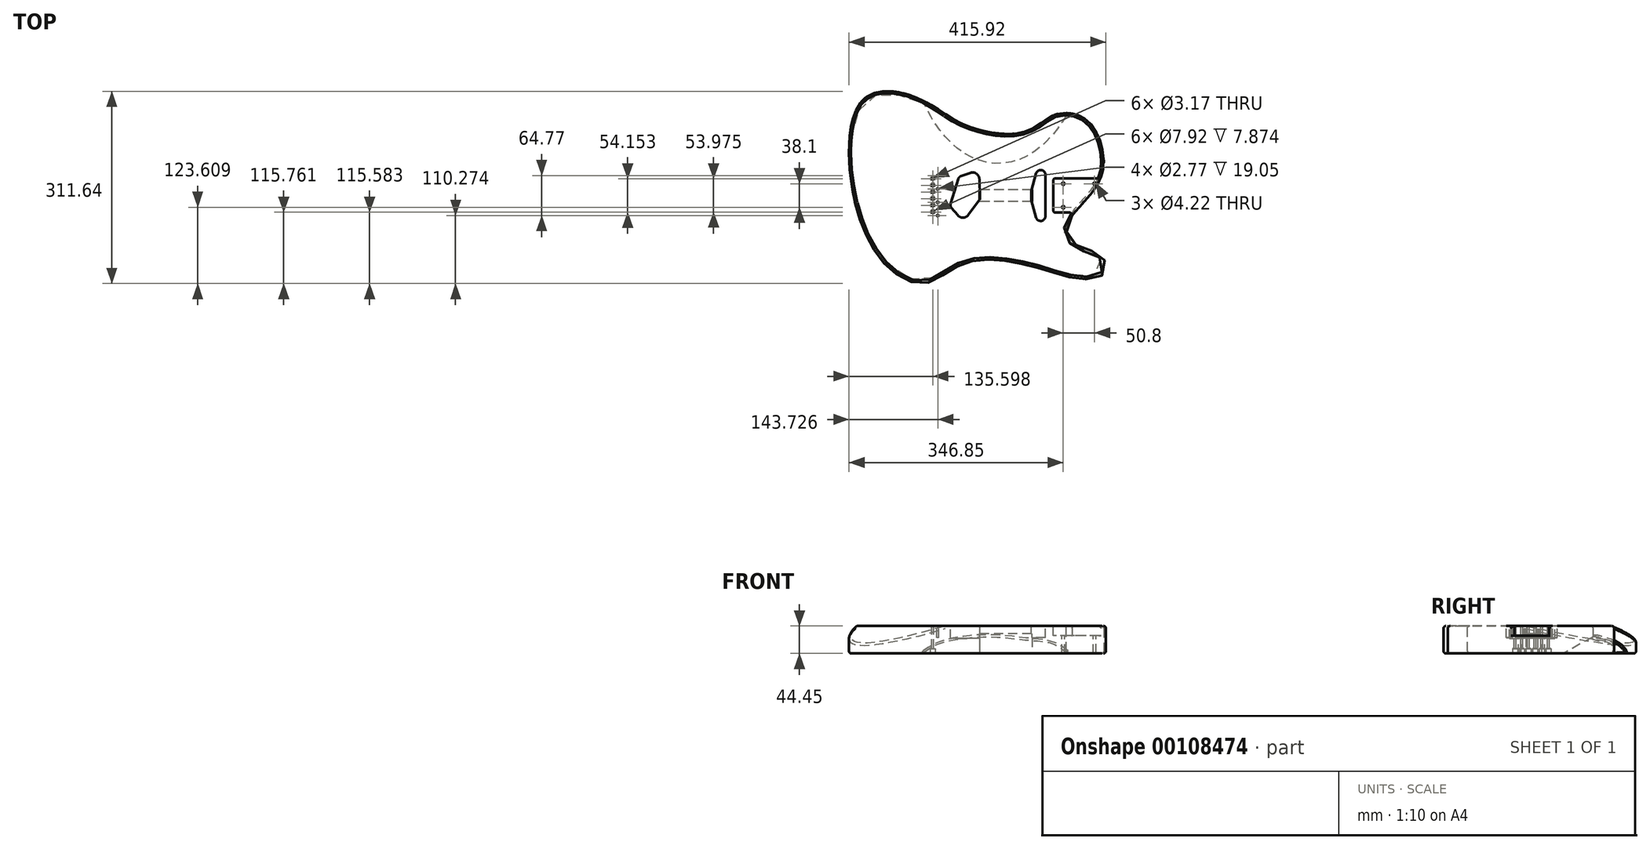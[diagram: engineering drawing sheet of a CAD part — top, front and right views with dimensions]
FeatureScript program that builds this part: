
annotation { "Feature Type Name" : "Feature", "Feature Type Description" : "" }
export const myFeature = defineFeature(function(context is Context, id is Id, definition is map)
    precondition{}
    {
        {
            var Q0;
            Q0=qCreatedBy(makeId("Top.planeOp"),FACE);
            var sketch = newSketch(context, id + "F0", { "sketchPlane" : qUnion([Q0])});
            skFitSpline(sketch, "E0", {"points": [v(437.8, 38.75) * mm, v(393.42, 31.36) * mm, v(332.63, 48.34) * mm, v(216.68, 57.77) * mm, v(157.53, 25.75) * mm, v(111.17, 32.37) * mm, v(43.17, 126.41) * mm, v(48.1, 320.57) * mm, v(140.27, 321.8) * mm, v(210.75, 280.95) * mm, v(303.47, 267.33) * mm, v(344.28, 288.4) * mm, v(367.26, 298.72) * mm, v(405.94, 290.75) * mm, v(432.67, 250.93) * mm, v(432.44, 193.48) * mm, v(390.48, 137.92) * mm, v(377.35, 108.2) * mm, v(396.27, 83.12) * mm, v(433.81, 68.33) * mm, v(437.8, 38.75) * mm]});
            skLineSegment(sketch, "E1", {"start": v(432.44, 193.48) * mm, "end": v(432.44, 137.92) * mm});
            skLineSegment(sketch, "E2", {"start": v(390.48, 137.92) * mm, "end": v(432.44, 137.92) * mm});
            skSolve(sketch);
        }
        {
            var Q0;
            Q0=makeQuery(id+"F0.imprint","IMPRINT",FACE,{"disambiguationData":[TD([[makeQuery(id+"F0.imprint","IMPRINT",EDGE,{"derivedFrom":sQuery(id+"F0.wireOp",EDGE,"E0")}),-1.0]])]});
            extrude(context, id + "F1", {"entities" : qUnion([Q0]), "depth" : 44.45 * mm});
        }
        {
            var Q0;
            Q0=qCreatedBy(makeId("Front.planeOp"),FACE);
            cPlane(context, id + "F2", {"entities" : qUnion([Q0]), "cplaneType" : CPlaneType.OFFSET, "offset" : 228.6 * mm, "oppositeDirection" : true, "width" : 152.4 * mm, "height" : 152.4 * mm});
        }
        {
            var Q0;
            Q0=qCreatedBy(id+"F2.planeOp",FACE);
            var sketch = newSketch(context, id + "F3", { "sketchPlane" : qUnion([Q0])});
            skLineSegment(sketch, "E3", {"start": v(7.53, 44.67) * mm, "end": v(7.53, 0) * mm});
            skSolve(sketch);
        }
        {
            var Q0;
            Q0=sQuery(id+"F3.wireOp",EDGE,"E3");
            var Q1;
            Q1=qCreatedBy(id+"F2.planeOp",FACE);
            cPlane(context, id + "F4", {"entities" : qUnion([Q0, Q1]), "cplaneType" : CPlaneType.LINE_ANGLE, "offset" : 25.4 * mm, "angle" : 45 * degree, "width" : 152.4 * mm, "height" : 152.4 * mm});
        }
        {
            var Q0;
            Q0=qCreatedBy(id+"F4.planeOp",FACE);
            var sketch = newSketch(context, id + "F5", { "sketchPlane" : qUnion([Q0])});
            skLineSegment(sketch, "E4", {"start": v(72.23, 46.82) * mm, "end": v(212.01, 11.13) * mm});
            skLineSegment(sketch, "E5.bottom", {"start": v(72.23, 46.82) * mm, "end": v(214.33, 45.27) * mm});
            skLineSegment(sketch, "E5.right", {"start": v(214.33, 45.27) * mm, "end": v(212.01, 11.13) * mm});
            skSolve(sketch);
        }
        {
            var Q0;
            Q0 = qSketchRegion(id + "F5", true);
            extrude(context, id + "F6", {"entities" : qUnion([Q0]), "operationType" : NewBodyOperationType.REMOVE, "endBound" : BoundingType.SYMMETRIC, "oppositeDirection" : true, "depth" : 508 * mm});
        }
        {
            var Q0;
            Q0=qCreatedBy(makeId("Right.planeOp"),FACE);
            cPlane(context, id + "F7", {"entities" : qUnion([Q0]), "cplaneType" : CPlaneType.OFFSET, "offset" : 266.7 * mm, "width" : 152.4 * mm, "height" : 152.4 * mm});
        }
        {
            var Q0;
            Q0=qCreatedBy(id+"F7.planeOp",FACE);
            var sketch = newSketch(context, id + "F8", { "sketchPlane" : qUnion([Q0])});
            skLineSegment(sketch, "E6", {"start": v(319.77, 57.36) * mm, "end": v(216.72, 0) * mm});
            skLineSegment(sketch, "E7", {"start": v(319.77, 57.36) * mm, "end": v(326.36, -7.5) * mm});
            skLineSegment(sketch, "E8", {"start": v(326.36, -7.5) * mm, "end": v(216.72, 0) * mm});
            skSolve(sketch);
        }
        {
            var Q0;
            Q0=qCreatedBy(id+"F7.planeOp",FACE);
            var sketch = newSketch(context, id + "F9", { "sketchPlane" : qUnion([Q0])});
            skLineSegment(sketch, "E9", {"start": v(470.03, -32.93) * mm, "end": v(353.93, -132.78) * mm});
            skSolve(sketch);
        }
        {
            var Q0;
            Q0=makeQuery(id+"F8.imprint","IMPRINT",FACE,{"disambiguationData":[TD([[makeQuery(id+"F8.imprint","IMPRINT",EDGE,{"derivedFrom":sQuery(id+"F8.wireOp",EDGE,"E6")}),1.0]])]});
            var Q1;
            Q1=sQuery(id+"F9.wireOp",EDGE,"E9");
            revolve(context, id + "F10", {"operationType" : NewBodyOperationType.REMOVE, "entities" : qUnion([Q0]), "axis" : qUnion([Q1]), "revolveType" : RevolveType.FULL, "oppositeDirection" : true});
        }
        {
            var Q0;
            Q0=makeQuery(id+"F1.opExtrude","CAP_FACE",FACE,{"disambiguationData":[OSD([sQuery(id+"F0.wireOp",EDGE,"E0"),sQuery(id+"F0.wireOp",EDGE,"E1"),sQuery(id+"F0.wireOp",EDGE,"E2")])],"isStart":false});
            var sketch = newSketch(context, id + "F11", { "sketchPlane" : qUnion([Q0])});
            skLineSegment(sketch, "E10.bottom", {"start": v(432.44, 137.92) * mm, "end": v(359.42, 137.92) * mm});
            skLineSegment(sketch, "E10.top", {"start": v(432.44, 193.48) * mm, "end": v(359.42, 193.48) * mm});
            skLineSegment(sketch, "E10.left", {"start": v(432.44, 137.92) * mm, "end": v(432.44, 193.48) * mm});
            skLineSegment(sketch, "E10.right", {"start": v(356.24, 141.1) * mm, "end": v(356.24, 190.3) * mm});
            skPoint(sketch, "E11.visualSharp", {"position": v(356.24, 193.48) * mm});
            skArc(sketch, "E11.filletArc", {"start": v(359.42, 193.48) * mm, "mid": v(357.17, 192.55) * mm, "end": v(356.24, 190.3) * mm});
            skPoint(sketch, "E12.visualSharp", {"position": v(356.24, 137.92) * mm});
            skArc(sketch, "E12.filletArc", {"start": v(356.24, 141.1) * mm, "mid": v(357.17, 138.85) * mm, "end": v(359.42, 137.92) * mm});
            skSolve(sketch);
        }
        {
            var Q0;
            Q0=makeQuery(id+"F11.imprint","IMPRINT",FACE,{"disambiguationData":[TD([[makeQuery(id+"F11.imprint","IMPRINT",EDGE,{"derivedFrom":sQuery(id+"F11.wireOp",EDGE,"E10.right")}),-1.0]])]});
            extrude(context, id + "F12", {"entities" : qUnion([Q0]), "operationType" : NewBodyOperationType.REMOVE, "oppositeDirection" : true, "depth" : 15.88 * mm});
        }
        {
            var Q0;
            Q0=makeQuery(id+"F1.opExtrude","CAP_FACE",FACE,{"disambiguationData":[OSD([sQuery(id+"F0.wireOp",EDGE,"E0"),sQuery(id+"F0.wireOp",EDGE,"E1"),sQuery(id+"F0.wireOp",EDGE,"E2")])],"isStart":false});
            var sketch = newSketch(context, id + "F13", { "sketchPlane" : qUnion([Q0])});
            skCircle(sketch, "E13", {"center": v(169.05, 198.08) * mm, "radius": 1.38 * mm});
            skCircle(sketch, "E14", {"center": v(169.05, 176.5) * mm, "radius": 1.38 * mm});
            skCircle(sketch, "E15", {"center": v(169.05, 154.9) * mm, "radius": 1.38 * mm});
            skCircle(sketch, "E16", {"center": v(169.05, 133.31) * mm, "radius": 1.38 * mm});
            skLineSegment(sketch, "E17", {"start": v(356.24, 165.7) * mm, "end": v(160.53, 165.7) * mm, "construction": true});
            skPoint(sketch, "E17.endSnap0", {"position": v(356.24, 165.7) * mm});
            skSolve(sketch);
        }
        {
            var Q0;
            Q0 = qSketchRegion(id + "F13", true);
            extrude(context, id + "F14", {"entities" : qUnion([Q0]), "operationType" : NewBodyOperationType.REMOVE, "oppositeDirection" : true, "depth" : 19.05 * mm});
        }
        {
            var Q0;
            Q0=makeQuery(id+"F1.opExtrude","CAP_FACE",FACE,{"disambiguationData":[OSD([sQuery(id+"F0.wireOp",EDGE,"E0"),sQuery(id+"F0.wireOp",EDGE,"E1"),sQuery(id+"F0.wireOp",EDGE,"E2")])],"isStart":false});
            var sketch = newSketch(context, id + "F15", { "sketchPlane" : qUnion([Q0])});
            skCircle(sketch, "E18", {"center": v(160.92, 192.78) * mm, "radius": 1.59 * mm});
            skLineSegment(sketch, "E19.direction1", {"start": v(160.92, 192.78) * mm, "end": v(162.5, 192.78) * mm, "construction": true});
            skLineSegment(sketch, "E20", {"start": v(356.24, 165.7) * mm, "end": v(102.22, 165.7) * mm, "construction": true});
            skLineSegment(sketch, "E21", {"start": v(169.05, 198.08) * mm, "end": v(169.05, 133.31) * mm, "construction": true});
            skCircle(sketch, "E22.0.1.0", {"center": v(160.92, 181.95) * mm, "radius": 1.59 * mm});
            skCircle(sketch, "E22.0.2.0", {"center": v(160.92, 171.11) * mm, "radius": 1.59 * mm});
            skCircle(sketch, "E22.0.3.0", {"center": v(160.92, 160.28) * mm, "radius": 1.59 * mm});
            skCircle(sketch, "E22.0.4.0", {"center": v(160.92, 149.45) * mm, "radius": 1.59 * mm});
            skCircle(sketch, "E22.0.5.0", {"center": v(160.92, 138.62) * mm, "radius": 1.59 * mm});
            skLineSegment(sketch, "E22.direction1", {"start": v(160.92, 192.78) * mm, "end": v(186.32, 192.78) * mm, "construction": true});
            skLineSegment(sketch, "E22.direction2", {"start": v(160.92, 192.78) * mm, "end": v(160.92, 181.95) * mm, "construction": true});
            skSolve(sketch);
        }
        {
            var Q0;
            Q0 = qSketchRegion(id + "F15", true);
            extrude(context, id + "F16", {"entities" : qUnion([Q0]), "operationType" : NewBodyOperationType.REMOVE, "endBound" : BoundingType.THROUGH_ALL, "oppositeDirection" : true, "depth" : 25.4 * mm});
        }
        {
            var Q0;
            Q0=makeQuery(id+"F1.opExtrude","CAP_FACE",FACE,{"disambiguationData":[OSD([sQuery(id+"F0.wireOp",EDGE,"E0"),sQuery(id+"F0.wireOp",EDGE,"E1"),sQuery(id+"F0.wireOp",EDGE,"E2")])],"isStart":true});
            var sketch = newSketch(context, id + "F17", { "sketchPlane" : qUnion([Q0])});
            skCircle(sketch, "E23", {"center": v(160.92, -192.78) * mm, "radius": 3.96 * mm});
            skCircle(sketch, "E24.0.1.0", {"center": v(160.92, -181.98) * mm, "radius": 3.96 * mm});
            skCircle(sketch, "E24.0.2.0", {"center": v(160.92, -171.19) * mm, "radius": 3.96 * mm});
            skCircle(sketch, "E24.0.3.0", {"center": v(160.92, -160.4) * mm, "radius": 3.96 * mm});
            skCircle(sketch, "E24.0.4.0", {"center": v(160.92, -149.6) * mm, "radius": 3.96 * mm});
            skCircle(sketch, "E24.0.5.0", {"center": v(160.92, -138.8) * mm, "radius": 3.96 * mm});
            skLineSegment(sketch, "E24.direction1", {"start": v(160.92, -192.78) * mm, "end": v(181.38, -192.78) * mm, "construction": true});
            skLineSegment(sketch, "E24.direction2", {"start": v(160.92, -181.98) * mm, "end": v(160.92, -192.78) * mm, "construction": true});
            skSolve(sketch);
        }
        {
            var Q0;
            Q0 = qSketchRegion(id + "F17", true);
            extrude(context, id + "F18", {"entities" : qUnion([Q0]), "operationType" : NewBodyOperationType.REMOVE, "oppositeDirection" : true, "depth" : 7.87 * mm});
        }
        {
            var Q0;
            Q0=makeQuery(id+"F1.opExtrude","CAP_FACE",FACE,{"disambiguationData":[OSD([sQuery(id+"F0.wireOp",EDGE,"E0"),sQuery(id+"F0.wireOp",EDGE,"E1"),sQuery(id+"F0.wireOp",EDGE,"E2")])],"isStart":false});
            var sketch = newSketch(context, id + "F19", { "sketchPlane" : qUnion([Q0])});
            skArc(sketch, "E25", {"start": v(236.4, 192.48) * mm, "mid": v(231.68, 201.04) * mm, "end": v(222, 202.4) * mm});
            skArc(sketch, "E26", {"start": v(201.44, 133.57) * mm, "mid": v(210.11, 129.73) * mm, "end": v(218.52, 134.12) * mm});
            skArc(sketch, "E27", {"start": v(206.93, 197.34) * mm, "mid": v(204.27, 195.67) * mm, "end": v(202.65, 192.96) * mm});
            skArc(sketch, "E28", {"start": v(189.87, 152.02) * mm, "mid": v(189.7, 148.67) * mm, "end": v(191.17, 145.66) * mm});
            skLineSegment(sketch, "E29", {"start": v(222, 202.4) * mm, "end": v(206.93, 197.34) * mm});
            skLineSegment(sketch, "E30", {"start": v(201.44, 133.57) * mm, "end": v(191.17, 145.66) * mm});
            skPoint(sketch, "E31.center.orphan", {"position": v(230.87, 162) * mm});
            skArc(sketch, "E32", {"start": v(236.27, 157.97) * mm, "mid": v(237.3, 160) * mm, "end": v(237.6, 162.26) * mm});
            skLineSegment(sketch, "E33", {"start": v(236.4, 192.48) * mm, "end": v(237.6, 162.26) * mm});
            skLineSegment(sketch, "E34", {"start": v(236.27, 157.97) * mm, "end": v(218.52, 134.12) * mm});
            skLineSegment(sketch, "E35", {"start": v(202.65, 192.96) * mm, "end": v(189.87, 152.02) * mm});
            skLineSegment(sketch, "E36", {"start": v(169.05, 133.31) * mm, "end": v(169.05, 198.08) * mm, "construction": true});
            skLineSegment(sketch, "E37", {"start": v(169.05, 165.7) * mm, "end": v(249.84, 165.7) * mm, "construction": true});
            skLineSegment(sketch, "E38", {"start": v(160.92, 138.62) * mm, "end": v(160.92, 192.78) * mm, "construction": true});
            skSolve(sketch);
        }
        {
            var Q0;
            Q0=makeQuery(id+"F19.imprint","IMPRINT",FACE,{"disambiguationData":[TD([[makeQuery(id+"F19.imprint","IMPRINT",EDGE,{"derivedFrom":sQuery(id+"F19.wireOp",EDGE,"E25")}),1.0]])]});
            extrude(context, id + "F20", {"entities" : qUnion([Q0]), "operationType" : NewBodyOperationType.REMOVE, "oppositeDirection" : true, "depth" : 20.32 * mm});
        }
        {
            var Q0;
            Q0=makeQuery(id+"F12.boolean.opBoolean","COPY",FACE,{"derivedFrom":makeQuery(id+"F12.opExtrude","CAP_FACE",FACE,{"disambiguationData":[OSD([sQuery(id+"F11.wireOp",EDGE,"E10.bottom"),sQuery(id+"F11.wireOp",EDGE,"E10.top"),sQuery(id+"F11.wireOp",EDGE,"E10.left"),sQuery(id+"F11.wireOp",EDGE,"E10.right"),sQuery(id+"F11.wireOp",EDGE,"E11.filletArc"),sQuery(id+"F11.wireOp",EDGE,"E12.filletArc")])],"isStart":false})});
            var sketch = newSketch(context, id + "F21", { "sketchPlane" : qUnion([Q0])});
            skCircle(sketch, "E39", {"center": v(372.17, 184.75) * mm, "radius": 2.1 * mm});
            skLineSegment(sketch, "E40", {"start": v(432.44, 165.7) * mm, "end": v(356.24, 165.7) * mm, "construction": true});
            skCircle(sketch, "E41.0.1.0", {"center": v(372.17, 146.65) * mm, "radius": 2.1 * mm});
            skCircle(sketch, "E41.1.0.0", {"center": v(422.97, 184.75) * mm, "radius": 2.1 * mm});
            skCircle(sketch, "E41.1.1.0", {"center": v(422.97, 146.65) * mm, "radius": 2.1 * mm});
            skLineSegment(sketch, "E41.direction1", {"start": v(372.17, 184.75) * mm, "end": v(422.97, 184.75) * mm, "construction": true});
            skLineSegment(sketch, "E41.direction2", {"start": v(372.17, 184.75) * mm, "end": v(372.17, 146.65) * mm, "construction": true});
            skSolve(sketch);
        }
        {
            var Q0;
            Q0 = qSketchRegion(id + "F21", true);
            extrude(context, id + "F22", {"entities" : qUnion([Q0]), "operationType" : NewBodyOperationType.REMOVE, "endBound" : BoundingType.THROUGH_ALL, "oppositeDirection" : true, "depth" : 25.4 * mm});
        }
        {
            var Q0;
            {var subQ0=sQuery(id+"F0.wireOp",EDGE,"E0");var subQ1=sQuery(id+"F0.wireOp",EDGE,"E1");Q0=makeQuery(id+"F6.boolean.opBoolean","SPLIT",EDGE,{"disambiguationData":[TD([makeQuery(id+"F1.opExtrude","SWEPT_FACE",FACE,{"disambiguationData":[OSD([subQ1])]})])],"derivedFrom":makeQuery(id+"F1.opExtrude","CAP_EDGE",EDGE,{"disambiguationData":[OSD([subQ0])],"isStart":false})});}
            var Q1;
            Q1=makeQuery(id+"F10.boolean.opBoolean","INTERSECT",EDGE,{"derivedFrom":[makeQuery(id+"F1.opExtrude","SWEPT_FACE",FACE,{"disambiguationData":[OSD([sQuery(id+"F0.wireOp",EDGE,"E0")])]}),makeQuery(id+"F10.opRevolve","SWEPT_FACE",FACE,{"disambiguationData":[OSD([sQuery(id+"F8.wireOp",EDGE,"E6")])]})]});
            var Q2;
            Q2=makeQuery(id+"F12.boolean.opBoolean","SPLIT",EDGE,{"derivedFrom":makeQuery(id+"F1.opExtrude","SWEPT_EDGE",EDGE,{"disambiguationData":[OSD([sQuery(id+"F0.wireOp",EDGE,"E0"),sQuery(id+"F0.wireOp",EDGE,"E1")])]})});
            var Q3;
            {var subQ0=sQuery(id+"F0.wireOp",EDGE,"E0");var subQ1=sQuery(id+"F0.wireOp",EDGE,"E2");Q3=makeQuery(id+"F10.boolean.opBoolean","SPLIT",EDGE,{"disambiguationData":[TD([makeQuery(id+"F1.opExtrude","SWEPT_FACE",FACE,{"disambiguationData":[OSD([subQ1])]})])],"derivedFrom":makeQuery(id+"F1.opExtrude","CAP_EDGE",EDGE,{"disambiguationData":[OSD([subQ0])],"isStart":true})});}
            var Q4;
            Q4=makeQuery(id+"F1.opExtrude","CAP_EDGE",EDGE,{"disambiguationData":[OSD([sQuery(id+"F0.wireOp",EDGE,"E1")])],"isStart":true});
            var Q5;
            Q5=makeQuery(id+"F1.opExtrude","SWEPT_EDGE",EDGE,{"disambiguationData":[OSD([sQuery(id+"F0.wireOp",EDGE,"E1"),sQuery(id+"F0.wireOp",EDGE,"E2")])]});
            var Q6;
            Q6=makeQuery(id+"F6.boolean.opBoolean","INTERSECT",EDGE,{"derivedFrom":[makeQuery(id+"F1.opExtrude","CAP_FACE",FACE,{"disambiguationData":[OSD([sQuery(id+"F0.wireOp",EDGE,"E0"),sQuery(id+"F0.wireOp",EDGE,"E1"),sQuery(id+"F0.wireOp",EDGE,"E2")])],"isStart":false}),makeQuery(id+"F6.opExtrude","SWEPT_FACE",FACE,{"disambiguationData":[OSD([sQuery(id+"F5.wireOp",EDGE,"E4")])]})]});
            var Q7;
            Q7=makeQuery(id+"F6.boolean.opBoolean","INTERSECT",EDGE,{"derivedFrom":[makeQuery(id+"F1.opExtrude","SWEPT_FACE",FACE,{"disambiguationData":[OSD([sQuery(id+"F0.wireOp",EDGE,"E0")])]}),makeQuery(id+"F6.opExtrude","SWEPT_FACE",FACE,{"disambiguationData":[OSD([sQuery(id+"F5.wireOp",EDGE,"E4")])]})]});
            var Q8;
            {var subQ0=sQuery(id+"F0.wireOp",EDGE,"E0");var subQ1=sQuery(id+"F0.wireOp",EDGE,"E1");Q8=makeQuery(id+"F10.boolean.opBoolean","SPLIT",EDGE,{"disambiguationData":[TD([makeQuery(id+"F1.opExtrude","SWEPT_FACE",FACE,{"disambiguationData":[OSD([subQ1])]})])],"derivedFrom":makeQuery(id+"F1.opExtrude","CAP_EDGE",EDGE,{"disambiguationData":[OSD([subQ0])],"isStart":true})});}
            var Q9;
            {var subQ0=sQuery(id+"F0.wireOp",EDGE,"E0");var subQ1=sQuery(id+"F0.wireOp",EDGE,"E2");Q9=makeQuery(id+"F6.boolean.opBoolean","SPLIT",EDGE,{"disambiguationData":[TD([makeQuery(id+"F1.opExtrude","SWEPT_FACE",FACE,{"disambiguationData":[OSD([subQ1])]})])],"derivedFrom":makeQuery(id+"F1.opExtrude","CAP_EDGE",EDGE,{"disambiguationData":[OSD([subQ0])],"isStart":false})});}
            var Q10;
            Q10=makeQuery(id+"F10.boolean.opBoolean","INTERSECT",EDGE,{"derivedFrom":[makeQuery(id+"F1.opExtrude","CAP_FACE",FACE,{"disambiguationData":[OSD([sQuery(id+"F0.wireOp",EDGE,"E0"),sQuery(id+"F0.wireOp",EDGE,"E1"),sQuery(id+"F0.wireOp",EDGE,"E2")])],"isStart":true}),makeQuery(id+"F10.opRevolve","SWEPT_FACE",FACE,{"disambiguationData":[OSD([sQuery(id+"F8.wireOp",EDGE,"E6")])]})]});
            var Q11;
            Q11=makeQuery(id+"F1.opExtrude","CAP_EDGE",EDGE,{"disambiguationData":[OSD([sQuery(id+"F0.wireOp",EDGE,"E2")])],"isStart":true});
            fillet(context, id + "F23", {"entities" : qUnion([Q0, Q1, Q2, Q3, Q4, Q5, Q6, Q7, Q8, Q9, Q10, Q11]), "radius" : 3.8 * mm, "tangentPropagation" : true, "allowEdgeOverflow" : false});
        }
        {
            var Q0;
            Q0=makeQuery(id+"F1.opExtrude","CAP_FACE",FACE,{"disambiguationData":[OSD([sQuery(id+"F0.wireOp",EDGE,"E0"),sQuery(id+"F0.wireOp",EDGE,"E1"),sQuery(id+"F0.wireOp",EDGE,"E2")])],"isStart":false});
            var sketch = newSketch(context, id + "F24", { "sketchPlane" : qUnion([Q0])});
            skLineSegment(sketch, "E42.right", {"start": v(343.29, 199.35) * mm, "end": v(343.29, 132.04) * mm});
            skArc(sketch, "E43", {"start": v(343.29, 199.35) * mm, "mid": v(336.71, 206.9) * mm, "end": v(328.33, 201.42) * mm});
            skArc(sketch, "E44", {"start": v(328.33, 129.98) * mm, "mid": v(336.71, 124.5) * mm, "end": v(343.29, 132.04) * mm});
            skLineSegment(sketch, "E45", {"start": v(356.24, 165.7) * mm, "end": v(275.02, 165.7) * mm, "construction": true});
            skLineSegment(sketch, "E46", {"start": v(320.43, 158.08) * mm, "end": v(328.33, 129.98) * mm});
            skLineSegment(sketch, "E47", {"start": v(320.43, 173.32) * mm, "end": v(328.33, 201.42) * mm});
            skLineSegment(sketch, "E48", {"start": v(320.43, 173.32) * mm, "end": v(320.43, 158.08) * mm});
            skPoint(sketch, "E49.orphan", {"position": v(328.05, 199.35) * mm});
            skPoint(sketch, "E50.orphan", {"position": v(328.05, 132.04) * mm});
            skSolve(sketch);
        }
        {
            var Q0;
            Q0 = qSketchRegion(id + "F24", true);
            extrude(context, id + "F25", {"entities" : qUnion([Q0]), "operationType" : NewBodyOperationType.REMOVE, "oppositeDirection" : true, "depth" : 19.05 * mm});
        }
        {
            var Q0;
            Q0=makeQuery(id+"F1.opExtrude","CAP_FACE",FACE,{"disambiguationData":[OSD([sQuery(id+"F0.wireOp",EDGE,"E0"),sQuery(id+"F0.wireOp",EDGE,"E1"),sQuery(id+"F0.wireOp",EDGE,"E2")])],"isStart":true});
            var sketch = newSketch(context, id + "F26", { "sketchPlane" : qUnion([Q0])});
            skLineSegment(sketch, "E51.bottom", {"start": v(321.95, -156.17) * mm, "end": v(236.86, -156.17) * mm});
            skLineSegment(sketch, "E51.top", {"start": v(321.95, -175.22) * mm, "end": v(236.86, -175.22) * mm});
            skLineSegment(sketch, "E51.left", {"start": v(321.95, -156.17) * mm, "end": v(321.95, -175.22) * mm});
            skLineSegment(sketch, "E51.right", {"start": v(236.86, -156.17) * mm, "end": v(236.86, -175.22) * mm});
            skLineSegment(sketch, "E52.0", {"start": v(356.24, -141.1) * mm, "end": v(356.24, -190.3) * mm, "construction": true});
            skLineSegment(sketch, "E53", {"start": v(356.24, -165.7) * mm, "end": v(194.73, -165.7) * mm, "construction": true});
            skSolve(sketch);
        }
        {
            var Q0;
            Q0=makeQuery(id+"F26.imprint","IMPRINT",FACE,{"disambiguationData":[TD([[makeQuery(id+"F26.imprint","IMPRINT",EDGE,{"derivedFrom":sQuery(id+"F26.wireOp",EDGE,"E51.bottom")}),1.0]])]});
            extrude(context, id + "F27", {"entities" : qUnion([Q0]), "operationType" : NewBodyOperationType.REMOVE, "oppositeDirection" : true, "depth" : 31.75 * mm});
        }
    });
